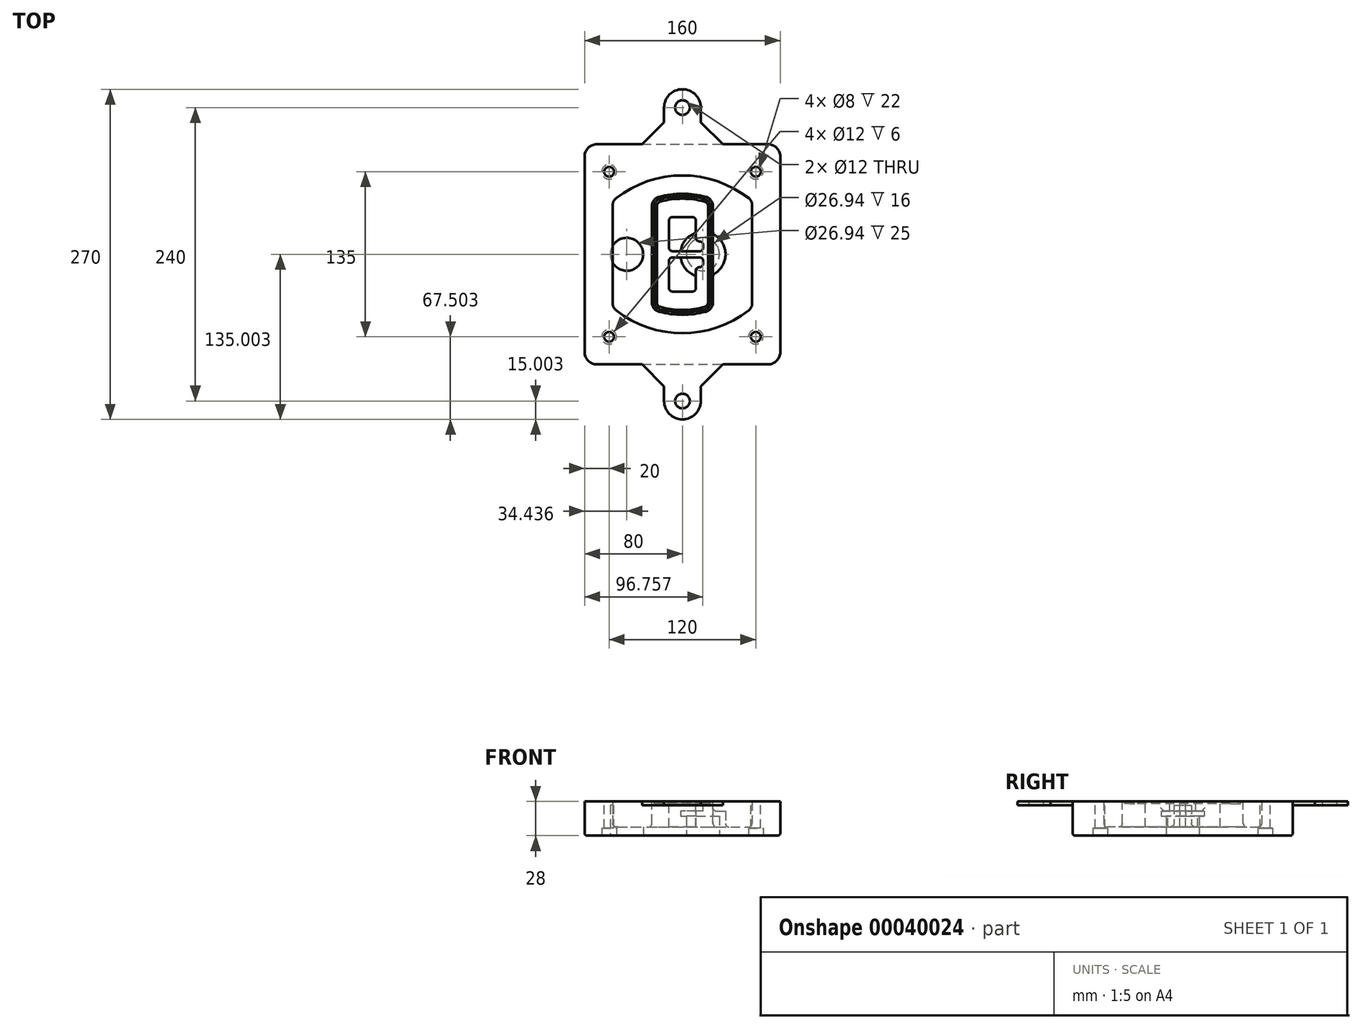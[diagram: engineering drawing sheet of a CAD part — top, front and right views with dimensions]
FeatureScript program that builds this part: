
annotation { "Feature Type Name" : "Feature", "Feature Type Description" : "" }
export const myFeature = defineFeature(function(context is Context, id is Id, definition is map)
    precondition{}
    {
        {
            var Q0;
            Q0=qCreatedBy(makeId("Top.planeOp"),FACE);
            var sketch = newSketch(context, id + "F0", { "sketchPlane" : qUnion([Q0])});
            skPoint(sketch, "E0.rect.middle", {"position": v(0, 0) * mm});
            skLineSegment(sketch, "E1.bottom", {"start": v(24.05, 28.38) * mm, "end": v(164.05, 28.38) * mm});
            skLineSegment(sketch, "E1.top", {"start": v(24.05, 208.38) * mm, "end": v(164.05, 208.38) * mm});
            skLineSegment(sketch, "E1.left", {"start": v(14.05, 38.38) * mm, "end": v(14.05, 198.38) * mm});
            skLineSegment(sketch, "E1.right", {"start": v(174.05, 38.38) * mm, "end": v(174.05, 198.38) * mm});
            skLineSegment(sketch, "E2", {"start": v(14.05, 208.38) * mm, "end": v(174.05, 28.38) * mm, "construction": true});
            skLineSegment(sketch, "E3", {"start": v(174.05, 208.38) * mm, "end": v(14.05, 28.38) * mm, "construction": true});
            skCircle(sketch, "E4", {"center": v(34.05, 185.88) * mm, "radius": 4 * mm});
            skCircle(sketch, "E5", {"center": v(154.05, 185.88) * mm, "radius": 4 * mm});
            skCircle(sketch, "E6", {"center": v(154.05, 50.88) * mm, "radius": 4 * mm});
            skCircle(sketch, "E7", {"center": v(34.05, 50.88) * mm, "radius": 4 * mm});
            skLineSegment(sketch, "E8", {"start": v(34.05, 185.88) * mm, "end": v(154.05, 185.88) * mm, "construction": true});
            skLineSegment(sketch, "E9", {"start": v(154.05, 185.88) * mm, "end": v(154.05, 50.88) * mm, "construction": true});
            skLineSegment(sketch, "E10", {"start": v(154.05, 50.88) * mm, "end": v(34.05, 50.88) * mm, "construction": true});
            skLineSegment(sketch, "E11", {"start": v(34.05, 50.88) * mm, "end": v(34.05, 185.88) * mm, "construction": true});
            skLineSegment(sketch, "E12", {"start": v(34.05, 158.68) * mm, "end": v(34.05, 78.09) * mm});
            skLineSegment(sketch, "E13", {"start": v(154.05, 158.68) * mm, "end": v(154.05, 78.09) * mm});
            skArc(sketch, "E14", {"start": v(150.2, 166.56) * mm, "mid": v(94.05, 185.88) * mm, "end": v(37.9, 166.56) * mm});
            skArc(sketch, "E15", {"start": v(37.9, 70.2) * mm, "mid": v(94.05, 50.88) * mm, "end": v(150.2, 70.2) * mm});
            skLineSegment(sketch, "E16", {"start": v(34.05, 118.38) * mm, "end": v(154.05, 118.38) * mm, "construction": true});
            skPoint(sketch, "E17.visualSharp", {"position": v(34.05, 73.38) * mm});
            skArc(sketch, "E17.filletArc", {"start": v(34.05, 78.09) * mm, "mid": v(35.06, 73.7) * mm, "end": v(37.9, 70.2) * mm});
            skPoint(sketch, "E18.visualSharp", {"position": v(34.05, 163.38) * mm});
            skArc(sketch, "E18.filletArc", {"start": v(37.9, 166.56) * mm, "mid": v(35.06, 163.06) * mm, "end": v(34.05, 158.68) * mm});
            skPoint(sketch, "E19.visualSharp", {"position": v(154.05, 163.38) * mm});
            skArc(sketch, "E19.filletArc", {"start": v(154.05, 158.68) * mm, "mid": v(153.04, 163.06) * mm, "end": v(150.2, 166.56) * mm});
            skPoint(sketch, "E20.visualSharp", {"position": v(154.05, 73.38) * mm});
            skArc(sketch, "E20.filletArc", {"start": v(150.2, 70.2) * mm, "mid": v(153.04, 73.7) * mm, "end": v(154.05, 78.09) * mm});
            skPoint(sketch, "E21.visualSharp", {"position": v(14.05, 208.38) * mm});
            skArc(sketch, "E21.filletArc", {"start": v(24.05, 208.38) * mm, "mid": v(16.98, 205.45) * mm, "end": v(14.05, 198.38) * mm});
            skPoint(sketch, "E22.visualSharp", {"position": v(174.05, 208.38) * mm});
            skArc(sketch, "E22.filletArc", {"start": v(174.05, 198.38) * mm, "mid": v(171.12, 205.45) * mm, "end": v(164.05, 208.38) * mm});
            skPoint(sketch, "E23.visualSharp", {"position": v(174.05, 28.38) * mm});
            skArc(sketch, "E23.filletArc", {"start": v(164.05, 28.38) * mm, "mid": v(171.12, 31.31) * mm, "end": v(174.05, 38.38) * mm});
            skPoint(sketch, "E24.visualSharp", {"position": v(14.05, 28.38) * mm});
            skArc(sketch, "E24.filletArc", {"start": v(14.05, 38.38) * mm, "mid": v(16.98, 31.31) * mm, "end": v(24.05, 28.38) * mm});
            skArc(sketch, "E25.0", {"start": v(151.05, 158.68) * mm, "mid": v(150.34, 161.75) * mm, "end": v(148.36, 164.2) * mm});
            skLineSegment(sketch, "E25.1", {"start": v(151.05, 158.68) * mm, "end": v(151.05, 78.09) * mm});
            skArc(sketch, "E25.2", {"start": v(148.36, 72.57) * mm, "mid": v(150.34, 75.02) * mm, "end": v(151.05, 78.09) * mm});
            skArc(sketch, "E25.3", {"start": v(39.74, 72.57) * mm, "mid": v(94.05, 53.88) * mm, "end": v(148.36, 72.57) * mm});
            skArc(sketch, "E25.4", {"start": v(37.05, 78.09) * mm, "mid": v(37.76, 75.02) * mm, "end": v(39.74, 72.57) * mm});
            skArc(sketch, "E25.5", {"start": v(148.36, 164.2) * mm, "mid": v(94.05, 182.88) * mm, "end": v(39.74, 164.2) * mm});
            skLineSegment(sketch, "E25.6", {"start": v(37.05, 158.68) * mm, "end": v(37.05, 78.09) * mm});
            skArc(sketch, "E25.7", {"start": v(39.74, 164.2) * mm, "mid": v(37.76, 161.75) * mm, "end": v(37.05, 158.68) * mm});
            skArc(sketch, "E26.0", {"start": v(35.43, 169.71) * mm, "mid": v(31.47, 164.82) * mm, "end": v(30.05, 158.68) * mm});
            skArc(sketch, "E26.1", {"start": v(152.67, 169.71) * mm, "mid": v(94.05, 189.88) * mm, "end": v(35.43, 169.71) * mm});
            skArc(sketch, "E26.2", {"start": v(158.05, 158.68) * mm, "mid": v(156.63, 164.82) * mm, "end": v(152.67, 169.71) * mm});
            skLineSegment(sketch, "E26.3", {"start": v(158.05, 158.68) * mm, "end": v(158.05, 78.09) * mm});
            skArc(sketch, "E26.4", {"start": v(152.67, 67.05) * mm, "mid": v(156.63, 71.95) * mm, "end": v(158.05, 78.09) * mm});
            skLineSegment(sketch, "E26.5", {"start": v(30.05, 158.68) * mm, "end": v(30.05, 78.09) * mm});
            skArc(sketch, "E26.6", {"start": v(35.43, 67.05) * mm, "mid": v(94.05, 46.88) * mm, "end": v(152.67, 67.05) * mm});
            skArc(sketch, "E26.7", {"start": v(30.05, 78.09) * mm, "mid": v(31.47, 71.95) * mm, "end": v(35.43, 67.05) * mm});
            skSolve(sketch);
        }
        {
            var Q0;
            Q0=makeQuery(id+"F0.imprint","IMPRINT",FACE,{"disambiguationData":[TD([[makeQuery(id+"F0.imprint","IMPRINT",EDGE,{"derivedFrom":sQuery(id+"F0.wireOp",EDGE,"E1.bottom")}),1.0]])]});
            var Q1;
            Q1=makeQuery(id+"F0.imprint","IMPRINT",FACE,{"disambiguationData":[TD([[makeQuery(id+"F0.imprint","IMPRINT",EDGE,{"derivedFrom":sQuery(id+"F0.wireOp",EDGE,"E12")}),1.0]])]});
            var Q2;
            Q2=makeQuery(id+"F0.imprint","IMPRINT",FACE,{"disambiguationData":[TD([[makeQuery(id+"F0.imprint","IMPRINT",EDGE,{"derivedFrom":sQuery(id+"F0.wireOp",EDGE,"E25.0")}),1.0]])]});
            var Q3;
            Q3=makeQuery(id+"F0.imprint","IMPRINT",FACE,{"disambiguationData":[TD([[makeQuery(id+"F0.imprint","IMPRINT",EDGE,{"derivedFrom":sQuery(id+"F0.wireOp",EDGE,"E12")}),-1.0]])]});
            extrude(context, id + "F1", {"entities" : qUnion([Q0, Q1, Q2, Q3]), "oppositeDirection" : true, "depth" : 25 * mm});
        }
        {
            var Q0;
            Q0=makeQuery(id+"F0.imprint","IMPRINT",FACE,{"disambiguationData":[TD([[makeQuery(id+"F0.imprint","IMPRINT",EDGE,{"derivedFrom":sQuery(id+"F0.wireOp",EDGE,"E12")}),1.0]])]});
            extrude(context, id + "F2", {"entities" : qUnion([Q0]), "operationType" : NewBodyOperationType.ADD, "depth" : 3 * mm});
        }
        {
            var Q0;
            Q0=makeQuery(id+"F0.imprint","IMPRINT",FACE,{"disambiguationData":[TD([[makeQuery(id+"F0.imprint","IMPRINT",EDGE,{"derivedFrom":sQuery(id+"F0.wireOp",EDGE,"E25.0")}),1.0]])]});
            extrude(context, id + "F3", {"entities" : qUnion([Q0]), "operationType" : NewBodyOperationType.REMOVE, "oppositeDirection" : true, "depth" : 18 * mm});
        }
        {
            var Q0;
            Q0=makeQuery(id+"F2.opExtrude","CAP_FACE",FACE,{"disambiguationData":[OSD([sQuery(id+"F0.wireOp",EDGE,"E12"),sQuery(id+"F0.wireOp",EDGE,"E13"),sQuery(id+"F0.wireOp",EDGE,"E14"),sQuery(id+"F0.wireOp",EDGE,"E15"),sQuery(id+"F0.wireOp",EDGE,"E17.filletArc"),sQuery(id+"F0.wireOp",EDGE,"E18.filletArc"),sQuery(id+"F0.wireOp",EDGE,"E19.filletArc"),sQuery(id+"F0.wireOp",EDGE,"E20.filletArc"),sQuery(id+"F0.wireOp",EDGE,"E25.0"),sQuery(id+"F0.wireOp",EDGE,"E25.1"),sQuery(id+"F0.wireOp",EDGE,"E25.2"),sQuery(id+"F0.wireOp",EDGE,"E25.3"),sQuery(id+"F0.wireOp",EDGE,"E25.4"),sQuery(id+"F0.wireOp",EDGE,"E25.5"),sQuery(id+"F0.wireOp",EDGE,"E25.6"),sQuery(id+"F0.wireOp",EDGE,"E25.7")])],"isStart":false});
            var sketch = newSketch(context, id + "F4", { "sketchPlane" : qUnion([Q0])});
            skArc(sketch, "E27.0", {"start": v(74.97, 71.41) * mm, "mid": v(94.05, 68.88) * mm, "end": v(113.13, 71.41) * mm});
            skArc(sketch, "E28.0", {"start": v(113.13, 165.35) * mm, "mid": v(94.05, 167.88) * mm, "end": v(74.97, 165.35) * mm});
            skLineSegment(sketch, "E29", {"start": v(69.05, 157.63) * mm, "end": v(69.05, 79.14) * mm});
            skLineSegment(sketch, "E30", {"start": v(119.05, 157.63) * mm, "end": v(119.05, 79.14) * mm});
            skLineSegment(sketch, "E31", {"start": v(69.05, 163.48) * mm, "end": v(119.05, 163.48) * mm, "construction": true});
            skLineSegment(sketch, "E32", {"start": v(69.05, 73.28) * mm, "end": v(119.05, 73.28) * mm, "construction": true});
            skPoint(sketch, "E33.visualSharp", {"position": v(69.05, 163.48) * mm});
            skArc(sketch, "E33.filletArc", {"start": v(74.97, 165.35) * mm, "mid": v(70.7, 162.5) * mm, "end": v(69.05, 157.63) * mm});
            skPoint(sketch, "E34.visualSharp", {"position": v(119.05, 163.48) * mm});
            skArc(sketch, "E34.filletArc", {"start": v(119.05, 157.63) * mm, "mid": v(117.4, 162.5) * mm, "end": v(113.13, 165.35) * mm});
            skPoint(sketch, "E35.visualSharp", {"position": v(119.05, 73.28) * mm});
            skArc(sketch, "E35.filletArc", {"start": v(113.13, 71.41) * mm, "mid": v(117.4, 74.27) * mm, "end": v(119.05, 79.14) * mm});
            skPoint(sketch, "E36.visualSharp", {"position": v(69.05, 73.28) * mm});
            skArc(sketch, "E36.filletArc", {"start": v(69.05, 79.14) * mm, "mid": v(70.7, 74.27) * mm, "end": v(74.97, 71.41) * mm});
            skArc(sketch, "E37.0", {"start": v(148.36, 164.2) * mm, "mid": v(94.05, 182.88) * mm, "end": v(39.74, 164.2) * mm});
            skArc(sketch, "E37.1", {"start": v(39.74, 164.2) * mm, "mid": v(37.76, 161.75) * mm, "end": v(37.05, 158.68) * mm});
            skLineSegment(sketch, "E37.2", {"start": v(37.05, 158.68) * mm, "end": v(37.05, 78.09) * mm});
            skArc(sketch, "E37.3", {"start": v(37.05, 78.09) * mm, "mid": v(37.76, 75.02) * mm, "end": v(39.74, 72.57) * mm});
            skArc(sketch, "E37.4", {"start": v(39.74, 72.57) * mm, "mid": v(94.05, 53.88) * mm, "end": v(148.36, 72.57) * mm});
            skArc(sketch, "E37.5", {"start": v(148.36, 72.57) * mm, "mid": v(150.34, 75.02) * mm, "end": v(151.05, 78.09) * mm});
            skLineSegment(sketch, "E37.6", {"start": v(151.05, 158.68) * mm, "end": v(151.05, 78.09) * mm});
            skArc(sketch, "E37.7", {"start": v(151.05, 158.68) * mm, "mid": v(150.34, 161.75) * mm, "end": v(148.36, 164.2) * mm});
            skLineSegment(sketch, "E38.0", {"start": v(117.05, 157.63) * mm, "end": v(117.05, 79.14) * mm});
            skArc(sketch, "E38.1", {"start": v(112.61, 73.34) * mm, "mid": v(115.81, 75.49) * mm, "end": v(117.05, 79.14) * mm});
            skArc(sketch, "E38.2", {"start": v(75.49, 73.34) * mm, "mid": v(94.05, 70.88) * mm, "end": v(112.61, 73.34) * mm});
            skArc(sketch, "E38.3", {"start": v(71.05, 79.14) * mm, "mid": v(72.29, 75.49) * mm, "end": v(75.49, 73.34) * mm});
            skLineSegment(sketch, "E38.4", {"start": v(71.05, 157.63) * mm, "end": v(71.05, 79.14) * mm});
            skArc(sketch, "E38.5", {"start": v(117.05, 157.63) * mm, "mid": v(115.81, 161.28) * mm, "end": v(112.61, 163.42) * mm});
            skArc(sketch, "E38.6", {"start": v(75.49, 163.42) * mm, "mid": v(72.29, 161.28) * mm, "end": v(71.05, 157.63) * mm});
            skArc(sketch, "E38.7", {"start": v(112.61, 163.42) * mm, "mid": v(94.05, 165.88) * mm, "end": v(75.49, 163.42) * mm});
            skArc(sketch, "E39.0", {"start": v(115.05, 157.63) * mm, "mid": v(114.23, 160.06) * mm, "end": v(112.1, 161.5) * mm});
            skLineSegment(sketch, "E39.1", {"start": v(115.05, 157.63) * mm, "end": v(115.05, 79.14) * mm});
            skArc(sketch, "E39.2", {"start": v(112.1, 75.27) * mm, "mid": v(114.23, 76.7) * mm, "end": v(115.05, 79.14) * mm});
            skArc(sketch, "E39.3", {"start": v(76, 75.27) * mm, "mid": v(94.05, 72.88) * mm, "end": v(112.1, 75.27) * mm});
            skArc(sketch, "E39.4", {"start": v(73.05, 79.14) * mm, "mid": v(73.87, 76.7) * mm, "end": v(76, 75.27) * mm});
            skArc(sketch, "E39.5", {"start": v(112.1, 161.5) * mm, "mid": v(94.05, 163.88) * mm, "end": v(76, 161.5) * mm});
            skLineSegment(sketch, "E39.6", {"start": v(73.05, 157.63) * mm, "end": v(73.05, 79.14) * mm});
            skArc(sketch, "E39.7", {"start": v(76, 161.5) * mm, "mid": v(73.87, 160.06) * mm, "end": v(73.05, 157.63) * mm});
            skLineSegment(sketch, "E40", {"start": v(69.05, 118.38) * mm, "end": v(119.05, 118.38) * mm, "construction": true});
            skLineSegment(sketch, "E41", {"start": v(83.05, 123.88) * mm, "end": v(83.05, 145.88) * mm});
            skLineSegment(sketch, "E42", {"start": v(86.05, 148.88) * mm, "end": v(102.05, 148.88) * mm});
            skLineSegment(sketch, "E43", {"start": v(105.05, 145.88) * mm, "end": v(105.05, 131.88) * mm});
            skLineSegment(sketch, "E44", {"start": v(108.05, 128.88) * mm, "end": v(108.05, 128.88) * mm});
            skLineSegment(sketch, "E45", {"start": v(111.05, 125.88) * mm, "end": v(111.05, 123.88) * mm});
            skLineSegment(sketch, "E46", {"start": v(108.05, 120.88) * mm, "end": v(86.05, 120.88) * mm});
            skPoint(sketch, "E47.visualSharp", {"position": v(83.05, 148.88) * mm});
            skArc(sketch, "E47.filletArc", {"start": v(86.05, 148.88) * mm, "mid": v(83.93, 148) * mm, "end": v(83.05, 145.88) * mm});
            skPoint(sketch, "E48.visualSharp", {"position": v(105.05, 148.88) * mm});
            skArc(sketch, "E48.filletArc", {"start": v(105.05, 145.88) * mm, "mid": v(104.17, 148) * mm, "end": v(102.05, 148.88) * mm});
            skPoint(sketch, "E49.visualSharp", {"position": v(105.05, 128.88) * mm});
            skArc(sketch, "E49.filletArc", {"start": v(105.05, 131.88) * mm, "mid": v(105.93, 129.76) * mm, "end": v(108.05, 128.88) * mm});
            skPoint(sketch, "E50.visualSharp", {"position": v(111.05, 128.88) * mm});
            skArc(sketch, "E50.filletArc", {"start": v(111.05, 125.88) * mm, "mid": v(110.17, 128) * mm, "end": v(108.05, 128.88) * mm});
            skPoint(sketch, "E51.visualSharp", {"position": v(111.05, 120.88) * mm});
            skArc(sketch, "E51.filletArc", {"start": v(108.05, 120.88) * mm, "mid": v(110.17, 121.76) * mm, "end": v(111.05, 123.88) * mm});
            skPoint(sketch, "E52.visualSharp", {"position": v(83.05, 120.88) * mm});
            skArc(sketch, "E52.filletArc", {"start": v(83.05, 123.88) * mm, "mid": v(83.93, 121.76) * mm, "end": v(86.05, 120.88) * mm});
            skLineSegment(sketch, "E53.0.MirrorCS", {"start": v(108.05, 115.88) * mm, "end": v(86.05, 115.88) * mm});
            skArc(sketch, "E54.0.MirrorCS", {"start": v(83.05, 112.88) * mm, "mid": v(83.93, 115) * mm, "end": v(86.05, 115.88) * mm});
            skLineSegment(sketch, "E55.0.MirrorCS", {"start": v(83.05, 112.88) * mm, "end": v(83.05, 90.88) * mm});
            skArc(sketch, "E56.0.MirrorCS", {"start": v(86.05, 87.88) * mm, "mid": v(83.93, 88.76) * mm, "end": v(83.05, 90.88) * mm});
            skLineSegment(sketch, "E57.0.MirrorCS", {"start": v(86.05, 87.88) * mm, "end": v(102.05, 87.88) * mm});
            skArc(sketch, "E58.0.MirrorCS", {"start": v(105.05, 90.88) * mm, "mid": v(104.17, 88.76) * mm, "end": v(102.05, 87.88) * mm});
            skLineSegment(sketch, "E59.0.MirrorCS", {"start": v(105.05, 90.88) * mm, "end": v(105.05, 104.88) * mm});
            skArc(sketch, "E60.0.MirrorCS", {"start": v(105.05, 104.88) * mm, "mid": v(105.93, 107) * mm, "end": v(108.05, 107.88) * mm});
            skArc(sketch, "E61.0.MirrorCS", {"start": v(111.05, 110.88) * mm, "mid": v(110.17, 108.76) * mm, "end": v(108.05, 107.88) * mm});
            skLineSegment(sketch, "E62.0.MirrorCS", {"start": v(111.05, 110.88) * mm, "end": v(111.05, 112.88) * mm});
            skArc(sketch, "E63.0.MirrorCS", {"start": v(108.05, 115.88) * mm, "mid": v(110.17, 115) * mm, "end": v(111.05, 112.88) * mm});
            skSolve(sketch);
        }
        {
            var Q0;
            Q0=makeQuery(id+"F4.imprint","IMPRINT",FACE,{"disambiguationData":[TD([[makeQuery(id+"F4.imprint","IMPRINT",EDGE,{"derivedFrom":sQuery(id+"F4.wireOp",EDGE,"E27.0")}),1.0]])]});
            var Q1;
            Q1=makeQuery(id+"F4.imprint","IMPRINT",FACE,{"disambiguationData":[TD([[makeQuery(id+"F4.imprint","IMPRINT",EDGE,{"derivedFrom":sQuery(id+"F4.wireOp",EDGE,"E38.0")}),-1.0]])]});
            var Q2;
            Q2=makeQuery(id+"F4.imprint","IMPRINT",FACE,{"disambiguationData":[TD([[makeQuery(id+"F4.imprint","IMPRINT",EDGE,{"derivedFrom":sQuery(id+"F4.wireOp",EDGE,"E39.0")}),1.0]])]});
            extrude(context, id + "F5", {"entities" : qUnion([Q0, Q1, Q2]), "operationType" : NewBodyOperationType.ADD, "endBound" : BoundingType.UP_TO_NEXT, "oppositeDirection" : true, "depth" : 25 * mm});
        }
        {
            var Q0;
            Q0=makeQuery(id+"F4.imprint","IMPRINT",FACE,{"disambiguationData":[TD([[makeQuery(id+"F4.imprint","IMPRINT",EDGE,{"derivedFrom":sQuery(id+"F4.wireOp",EDGE,"E38.0")}),-1.0]])]});
            extrude(context, id + "F6", {"entities" : qUnion([Q0]), "operationType" : NewBodyOperationType.REMOVE, "oppositeDirection" : true, "depth" : 2 * mm});
        }
        {
            var Q0;
            Q0=makeQuery(id+"F1.opExtrude","CAP_FACE",FACE,{"disambiguationData":[OSD([sQuery(id+"F0.wireOp",EDGE,"E1.bottom"),sQuery(id+"F0.wireOp",EDGE,"E1.top"),sQuery(id+"F0.wireOp",EDGE,"E1.left"),sQuery(id+"F0.wireOp",EDGE,"E1.right"),sQuery(id+"F0.wireOp",EDGE,"E4"),sQuery(id+"F0.wireOp",EDGE,"E5"),sQuery(id+"F0.wireOp",EDGE,"E6"),sQuery(id+"F0.wireOp",EDGE,"E7"),sQuery(id+"F0.wireOp",EDGE,"E21.filletArc"),sQuery(id+"F0.wireOp",EDGE,"E22.filletArc"),sQuery(id+"F0.wireOp",EDGE,"E23.filletArc"),sQuery(id+"F0.wireOp",EDGE,"E24.filletArc")])],"isStart":false});
            var sketch = newSketch(context, id + "F7", { "sketchPlane" : qUnion([Q0])});
            skCircle(sketch, "E64", {"center": v(110.8, -118.38) * mm, "radius": 13.47 * mm});
            skCircle(sketch, "E65", {"center": v(48.49, -118.38) * mm, "radius": 13.47 * mm});
            skLineSegment(sketch, "E66", {"start": v(174.05, -118.38) * mm, "end": v(14.05, -118.38) * mm});
            skCircle(sketch, "E67", {"center": v(110.8, -118.38) * mm, "radius": 18.47 * mm});
            skCircle(sketch, "E68", {"center": v(154.05, -185.88) * mm, "radius": 6 * mm});
            skCircle(sketch, "E69", {"center": v(34.05, -185.88) * mm, "radius": 6 * mm});
            skCircle(sketch, "E70", {"center": v(34.05, -50.88) * mm, "radius": 6 * mm});
            skCircle(sketch, "E71", {"center": v(154.05, -50.88) * mm, "radius": 6 * mm});
            skSolve(sketch);
        }
        {
            var Q0;
            {var subQ1=sQuery(id+"F7.wireOp",EDGE,"E66");var subQ4=sQuery(id+"F7.wireOp",EDGE,"E64");var subQ6=makeQuery(id+"F7.imprint","INTERSECT",VERTEX,{"disambiguationData":[OD(0.0)],"derivedFrom":[subQ4,subQ1]});Q0=makeQuery(id+"F7.imprint","IMPRINT",FACE,{"disambiguationData":[TD([[makeQuery(id+"F7.imprint","IMPRINT",EDGE,{"disambiguationData":[TD([[subQ6,-1.0]])],"derivedFrom":subQ4}),-1.0]])]});}
            var Q1;
            {var subQ0=sQuery(id+"F7.wireOp",EDGE,"E66");var subQ1=sQuery(id+"F7.wireOp",EDGE,"E64");var subQ3=makeQuery(id+"F7.imprint","INTERSECT",VERTEX,{"disambiguationData":[OD(0.0)],"derivedFrom":[subQ1,subQ0]});Q1=makeQuery(id+"F7.imprint","IMPRINT",FACE,{"disambiguationData":[TD([[makeQuery(id+"F7.imprint","IMPRINT",EDGE,{"disambiguationData":[TD([[subQ3,-1.0]])],"derivedFrom":subQ1}),1.0]])]});}
            var Q2;
            {var subQ0=sQuery(id+"F7.wireOp",EDGE,"E66");var subQ1=sQuery(id+"F7.wireOp",EDGE,"E64");var subQ3=makeQuery(id+"F7.imprint","INTERSECT",VERTEX,{"disambiguationData":[OD(0.0)],"derivedFrom":[subQ1,subQ0]});Q2=makeQuery(id+"F7.imprint","IMPRINT",FACE,{"disambiguationData":[TD([[makeQuery(id+"F7.imprint","IMPRINT",EDGE,{"disambiguationData":[TD([[subQ3,1.0]])],"derivedFrom":subQ1}),1.0]])]});}
            var Q3;
            {var subQ1=sQuery(id+"F7.wireOp",EDGE,"E66");var subQ4=sQuery(id+"F7.wireOp",EDGE,"E64");var subQ6=makeQuery(id+"F7.imprint","INTERSECT",VERTEX,{"disambiguationData":[OD(0.0)],"derivedFrom":[subQ4,subQ1]});Q3=makeQuery(id+"F7.imprint","IMPRINT",FACE,{"disambiguationData":[TD([[makeQuery(id+"F7.imprint","IMPRINT",EDGE,{"disambiguationData":[TD([[subQ6,1.0]])],"derivedFrom":subQ4}),-1.0]])]});}
            extrude(context, id + "F8", {"entities" : qUnion([Q0, Q1, Q2, Q3]), "operationType" : NewBodyOperationType.ADD, "oppositeDirection" : true, "depth" : 20 * mm});
        }
        {
            var Q0;
            {var subQ0=sQuery(id+"F7.wireOp",EDGE,"E66");var subQ1=sQuery(id+"F7.wireOp",EDGE,"E64");var subQ3=makeQuery(id+"F7.imprint","INTERSECT",VERTEX,{"disambiguationData":[OD(0.0)],"derivedFrom":[subQ1,subQ0]});Q0=makeQuery(id+"F7.imprint","IMPRINT",FACE,{"disambiguationData":[TD([[makeQuery(id+"F7.imprint","IMPRINT",EDGE,{"disambiguationData":[TD([[subQ3,-1.0]])],"derivedFrom":subQ1}),1.0]])]});}
            var Q1;
            {var subQ0=sQuery(id+"F7.wireOp",EDGE,"E66");var subQ1=sQuery(id+"F7.wireOp",EDGE,"E64");var subQ3=makeQuery(id+"F7.imprint","INTERSECT",VERTEX,{"disambiguationData":[OD(0.0)],"derivedFrom":[subQ1,subQ0]});Q1=makeQuery(id+"F7.imprint","IMPRINT",FACE,{"disambiguationData":[TD([[makeQuery(id+"F7.imprint","IMPRINT",EDGE,{"disambiguationData":[TD([[subQ3,1.0]])],"derivedFrom":subQ1}),1.0]])]});}
            extrude(context, id + "F9", {"entities" : qUnion([Q0, Q1]), "operationType" : NewBodyOperationType.REMOVE, "oppositeDirection" : true, "depth" : 16 * mm});
        }
        {
            var Q0;
            {var subQ0=sQuery(id+"F7.wireOp",EDGE,"E66");var subQ1=sQuery(id+"F7.wireOp",EDGE,"E65");var subQ3=makeQuery(id+"F7.imprint","INTERSECT",VERTEX,{"disambiguationData":[OD(0.0)],"derivedFrom":[subQ1,subQ0]});Q0=makeQuery(id+"F7.imprint","IMPRINT",FACE,{"disambiguationData":[TD([[makeQuery(id+"F7.imprint","IMPRINT",EDGE,{"disambiguationData":[TD([[subQ3,-1.0]])],"derivedFrom":subQ1}),1.0]])]});}
            var Q1;
            {var subQ0=sQuery(id+"F7.wireOp",EDGE,"E66");var subQ1=sQuery(id+"F7.wireOp",EDGE,"E65");var subQ3=makeQuery(id+"F7.imprint","INTERSECT",VERTEX,{"disambiguationData":[OD(0.0)],"derivedFrom":[subQ1,subQ0]});Q1=makeQuery(id+"F7.imprint","IMPRINT",FACE,{"disambiguationData":[TD([[makeQuery(id+"F7.imprint","IMPRINT",EDGE,{"disambiguationData":[TD([[subQ3,1.0]])],"derivedFrom":subQ1}),1.0]])]});}
            extrude(context, id + "F10", {"entities" : qUnion([Q0, Q1]), "operationType" : NewBodyOperationType.REMOVE, "oppositeDirection" : true, "depth" : 25 * mm});
        }
        {
            var Q0;
            Q0=makeQuery(id+"F7.imprint","IMPRINT",FACE,{"disambiguationData":[TD([[makeQuery(id+"F7.imprint","IMPRINT",EDGE,{"derivedFrom":sQuery(id+"F7.wireOp",EDGE,"E68")}),1.0]])]});
            var Q1;
            Q1=makeQuery(id+"F7.imprint","IMPRINT",FACE,{"disambiguationData":[TD([[makeQuery(id+"F7.imprint","IMPRINT",EDGE,{"derivedFrom":makeQuery(id+"F1.opExtrude","CAP_EDGE",EDGE,{"disambiguationData":[OSD([sQuery(id+"F0.wireOp",EDGE,"E5")])],"isStart":false})}),-1.0]])]});
            var Q2;
            Q2=makeQuery(id+"F7.imprint","IMPRINT",FACE,{"disambiguationData":[TD([[makeQuery(id+"F7.imprint","IMPRINT",EDGE,{"derivedFrom":sQuery(id+"F7.wireOp",EDGE,"E69")}),1.0]])]});
            var Q3;
            Q3=makeQuery(id+"F7.imprint","IMPRINT",FACE,{"disambiguationData":[TD([[makeQuery(id+"F7.imprint","IMPRINT",EDGE,{"derivedFrom":makeQuery(id+"F1.opExtrude","CAP_EDGE",EDGE,{"disambiguationData":[OSD([sQuery(id+"F0.wireOp",EDGE,"E4")])],"isStart":false})}),-1.0]])]});
            var Q4;
            Q4=makeQuery(id+"F7.imprint","IMPRINT",FACE,{"disambiguationData":[TD([[makeQuery(id+"F7.imprint","IMPRINT",EDGE,{"derivedFrom":sQuery(id+"F7.wireOp",EDGE,"E70")}),1.0]])]});
            var Q5;
            Q5=makeQuery(id+"F7.imprint","IMPRINT",FACE,{"disambiguationData":[TD([[makeQuery(id+"F7.imprint","IMPRINT",EDGE,{"derivedFrom":makeQuery(id+"F1.opExtrude","CAP_EDGE",EDGE,{"disambiguationData":[OSD([sQuery(id+"F0.wireOp",EDGE,"E7")])],"isStart":false})}),-1.0]])]});
            var Q6;
            Q6=makeQuery(id+"F7.imprint","IMPRINT",FACE,{"disambiguationData":[TD([[makeQuery(id+"F7.imprint","IMPRINT",EDGE,{"derivedFrom":sQuery(id+"F7.wireOp",EDGE,"E71")}),1.0]])]});
            var Q7;
            Q7=makeQuery(id+"F7.imprint","IMPRINT",FACE,{"disambiguationData":[TD([[makeQuery(id+"F7.imprint","IMPRINT",EDGE,{"derivedFrom":makeQuery(id+"F1.opExtrude","CAP_EDGE",EDGE,{"disambiguationData":[OSD([sQuery(id+"F0.wireOp",EDGE,"E6")])],"isStart":false})}),-1.0]])]});
            extrude(context, id + "F11", {"entities" : qUnion([Q0, Q1, Q2, Q3, Q4, Q5, Q6, Q7]), "operationType" : NewBodyOperationType.REMOVE, "oppositeDirection" : true, "depth" : 6 * mm});
        }
        {
            var Q0;
            Q0=makeQuery(id+"F9.boolean.opBoolean","COPY",FACE,{"derivedFrom":makeQuery(id+"F9.opExtrude","CAP_FACE",FACE,{"disambiguationData":[OSD([sQuery(id+"F7.wireOp",EDGE,"E64")])],"isStart":false})});
            var sketch = newSketch(context, id + "F12", { "sketchPlane" : qUnion([Q0])});
            skArc(sketch, "E72.0", {"start": v(105.05, -100.83) * mm, "mid": v(96.62, -106.56) * mm, "end": v(92.5, -115.88) * mm});
            skArc(sketch, "E72.1", {"start": v(92.5, -120.88) * mm, "mid": v(96.62, -130.2) * mm, "end": v(105.05, -135.93) * mm});
            skLineSegment(sketch, "E73", {"start": v(92.5, -120.88) * mm, "end": v(108.05, -120.88) * mm});
            skLineSegment(sketch, "E74.0", {"start": v(108.05, -115.88) * mm, "end": v(92.5, -115.88) * mm});
            skArc(sketch, "E74.1", {"start": v(108.05, -115.88) * mm, "mid": v(110.17, -115) * mm, "end": v(111.05, -112.88) * mm});
            skLineSegment(sketch, "E74.2", {"start": v(111.05, -110.88) * mm, "end": v(111.05, -112.88) * mm});
            skArc(sketch, "E74.3", {"start": v(111.05, -110.88) * mm, "mid": v(110.17, -108.76) * mm, "end": v(108.05, -107.88) * mm});
            skArc(sketch, "E74.4", {"start": v(105.05, -104.88) * mm, "mid": v(105.93, -107) * mm, "end": v(108.05, -107.88) * mm});
            skLineSegment(sketch, "E74.5", {"start": v(105.05, -100.83) * mm, "end": v(105.05, -104.88) * mm});
            skLineSegment(sketch, "E74.7", {"start": v(108.05, -120.88) * mm, "end": v(92.5, -120.88) * mm});
            skArc(sketch, "E74.8", {"start": v(108.05, -120.88) * mm, "mid": v(110.17, -121.76) * mm, "end": v(111.05, -123.88) * mm});
            skLineSegment(sketch, "E74.9", {"start": v(111.05, -125.88) * mm, "end": v(111.05, -123.88) * mm});
            skArc(sketch, "E74.10", {"start": v(111.05, -125.88) * mm, "mid": v(110.17, -128) * mm, "end": v(108.05, -128.88) * mm});
            skArc(sketch, "E74.11", {"start": v(105.05, -131.88) * mm, "mid": v(105.93, -129.76) * mm, "end": v(108.05, -128.88) * mm});
            skLineSegment(sketch, "E74.12", {"start": v(105.05, -135.93) * mm, "end": v(105.05, -131.88) * mm});
            skPoint(sketch, "E75.orphan", {"position": v(105.05, -145.88) * mm});
            skPoint(sketch, "E76.orphan", {"position": v(86.05, -120.88) * mm});
            skPoint(sketch, "E77.orphan", {"position": v(86.05, -115.88) * mm});
            skPoint(sketch, "E78.orphan", {"position": v(105.05, -90.88) * mm});
            skSolve(sketch);
        }
        {
            var Q0;
            {var subQ7=sQuery(id+"F12.wireOp",EDGE,"E72.0");var subQ14=sQuery(id+"F12.wireOp",EDGE,"E72.1");var subQ16=sQuery(id+"F12.wireOp",EDGE,"E74.1");var subQ18=sQuery(id+"F12.wireOp",EDGE,"E74.8");Q0=qUnion([makeQuery(id+"F12.imprint","IMPRINT",FACE,{"disambiguationData":[TD([[makeQuery(id+"F12.imprint","IMPRINT",EDGE,{"derivedFrom":subQ7}),1.0]])]}),makeQuery(id+"F12.imprint","IMPRINT",FACE,{"disambiguationData":[TD([[makeQuery(id+"F12.imprint","IMPRINT",EDGE,{"derivedFrom":subQ14}),1.0]])]}),makeQuery(id+"F12.imprint","IMPRINT",FACE,{"disambiguationData":[TD([[makeQuery(id+"F12.imprint","IMPRINT",EDGE,{"derivedFrom":subQ16}),1.0]])]}),makeQuery(id+"F12.imprint","IMPRINT",FACE,{"disambiguationData":[TD([[makeQuery(id+"F12.imprint","IMPRINT",EDGE,{"derivedFrom":subQ18}),-1.0]])]})]);}
            var Q1;
            Q1=makeQuery(id+"F5.boolean.opBoolean","SPLIT",FACE,{"disambiguationData":[TD([makeQuery(id+"F5.opExtrude","SWEPT_FACE",FACE,{"disambiguationData":[OSD([sQuery(id+"F4.wireOp",EDGE,"E41")])]})])],"derivedFrom":makeQuery(id+"F3.boolean.opBoolean","COPY",FACE,{"derivedFrom":makeQuery(id+"F3.opExtrude","CAP_FACE",FACE,{"disambiguationData":[OSD([sQuery(id+"F0.wireOp",EDGE,"E25.0"),sQuery(id+"F0.wireOp",EDGE,"E25.1"),sQuery(id+"F0.wireOp",EDGE,"E25.2"),sQuery(id+"F0.wireOp",EDGE,"E25.3"),sQuery(id+"F0.wireOp",EDGE,"E25.4"),sQuery(id+"F0.wireOp",EDGE,"E25.5"),sQuery(id+"F0.wireOp",EDGE,"E25.6"),sQuery(id+"F0.wireOp",EDGE,"E25.7")])],"isStart":false})})});
            extrude(context, id + "F13", {"entities" : qUnion([Q0]), "operationType" : NewBodyOperationType.REMOVE, "endBound" : BoundingType.UP_TO_SURFACE, "endBoundEntityFace" : qUnion([Q1]), "depth" : 25 * mm});
        }
        {
            var Q0;
            Q0=makeQuery(id+"F3.boolean.opBoolean","COPY",EDGE,{"derivedFrom":makeQuery(id+"F3.opExtrude","CAP_EDGE",EDGE,{"disambiguationData":[OSD([sQuery(id+"F0.wireOp",EDGE,"E25.6")])],"isStart":false})});
            var Q1;
            Q1=makeQuery(id+"F8.boolean.opBoolean","INTERSECT",EDGE,{"derivedFrom":[makeQuery(id+"F5.opExtrude","SWEPT_FACE",FACE,{"disambiguationData":[OSD([sQuery(id+"F4.wireOp",EDGE,"E30")])]}),makeQuery(id+"F8.opExtrude","CAP_FACE",FACE,{"disambiguationData":[OSD([sQuery(id+"F7.wireOp",EDGE,"E67")])],"isStart":false})]});
            var Q2;
            Q2=makeQuery(id+"F8.boolean.opBoolean","INTERSECT",EDGE,{"disambiguationData":[OD(1.0)],"derivedFrom":[makeQuery(id+"F5.opExtrude","SWEPT_FACE",FACE,{"disambiguationData":[OSD([sQuery(id+"F4.wireOp",EDGE,"E30")])]}),makeQuery(id+"F8.opExtrude","SWEPT_FACE",FACE,{"disambiguationData":[OSD([sQuery(id+"F7.wireOp",EDGE,"E67")])]})]});
            var Q3;
            {var subQ0=sQuery(id+"F4.wireOp",EDGE,"E30");Q3=makeQuery(id+"F8.boolean.opBoolean","SPLIT",EDGE,{"disambiguationData":[TD([makeQuery(id+"F5.opExtrude","SWEPT_FACE",FACE,{"disambiguationData":[OSD([sQuery(id+"F4.wireOp",EDGE,"E35.filletArc")])]})])],"derivedFrom":makeQuery(id+"F5.opExtrude","CAP_EDGE",EDGE,{"disambiguationData":[OSD([subQ0])],"isStart":false})});}
            var Q4;
            {var subQ0=sQuery(id+"F0.wireOp",EDGE,"E25.7");var subQ1=sQuery(id+"F0.wireOp",EDGE,"E25.1");var subQ2=sQuery(id+"F0.wireOp",EDGE,"E25.6");var subQ3=sQuery(id+"F0.wireOp",EDGE,"E25.5");var subQ4=sQuery(id+"F0.wireOp",EDGE,"E25.4");var subQ5=sQuery(id+"F0.wireOp",EDGE,"E25.0");var subQ6=sQuery(id+"F0.wireOp",EDGE,"E25.2");var subQ7=sQuery(id+"F0.wireOp",EDGE,"E25.3");Q4=makeQuery(id+"F8.boolean.opBoolean","INTERSECT",EDGE,{"derivedFrom":[makeQuery(id+"F5.boolean.opBoolean","SPLIT",FACE,{"disambiguationData":[TD([makeQuery(id+"F2.opExtrude","SWEPT_FACE",FACE,{"disambiguationData":[OSD([subQ5])]})])],"derivedFrom":makeQuery(id+"F3.boolean.opBoolean","COPY",FACE,{"derivedFrom":makeQuery(id+"F3.opExtrude","CAP_FACE",FACE,{"disambiguationData":[OSD([subQ5,subQ1,subQ6,subQ7,subQ4,subQ3,subQ2,subQ0])],"isStart":false})})}),makeQuery(id+"F8.opExtrude","SWEPT_FACE",FACE,{"disambiguationData":[OSD([sQuery(id+"F7.wireOp",EDGE,"E67")])]})]});}
            var Q5;
            Q5=makeQuery(id+"F8.boolean.opBoolean","INTERSECT",EDGE,{"disambiguationData":[OD(0.0)],"derivedFrom":[makeQuery(id+"F5.opExtrude","SWEPT_FACE",FACE,{"disambiguationData":[OSD([sQuery(id+"F4.wireOp",EDGE,"E30")])]}),makeQuery(id+"F8.opExtrude","SWEPT_FACE",FACE,{"disambiguationData":[OSD([sQuery(id+"F7.wireOp",EDGE,"E67")])]})]});
            fillet(context, id + "F14", {"entities" : qUnion([Q0, Q1, Q2, Q3, Q4, Q5]), "radius" : 3 * mm, "tangentPropagation" : true, "allowEdgeOverflow" : false});
        }
        {
            var Q0;
            Q0=makeQuery(id+"F1.opExtrude","CAP_EDGE",EDGE,{"disambiguationData":[OSD([sQuery(id+"F0.wireOp",EDGE,"E1.bottom")])],"isStart":false});
            fillet(context, id + "F15", {"entities" : qUnion([Q0]), "radius" : 2 * mm, "tangentPropagation" : true, "allowEdgeOverflow" : false});
        }
        {
            var Q0;
            {var subQ0=sQuery(id+"F0.wireOp",EDGE,"E1.bottom");var subQ1=sQuery(id+"F0.wireOp",EDGE,"E1.top");var subQ2=sQuery(id+"F0.wireOp",EDGE,"E1.left");var subQ3=sQuery(id+"F0.wireOp",EDGE,"E1.right");var subQ4=sQuery(id+"F0.wireOp",EDGE,"E4");var subQ5=sQuery(id+"F0.wireOp",EDGE,"E5");var subQ6=sQuery(id+"F0.wireOp",EDGE,"E6");var subQ7=sQuery(id+"F0.wireOp",EDGE,"E7");var subQ8=sQuery(id+"F0.wireOp",EDGE,"E21.filletArc");var subQ9=sQuery(id+"F0.wireOp",EDGE,"E22.filletArc");var subQ10=sQuery(id+"F0.wireOp",EDGE,"E23.filletArc");var subQ11=sQuery(id+"F0.wireOp",EDGE,"E24.filletArc");Q0=makeQuery(id+"F2.boolean.opBoolean","SPLIT",FACE,{"disambiguationData":[TD([makeQuery(id+"F1.opExtrude","SWEPT_FACE",FACE,{"disambiguationData":[OSD([subQ0])]})])],"derivedFrom":makeQuery(id+"F1.opExtrude","CAP_FACE",FACE,{"disambiguationData":[OSD([subQ0,subQ1,subQ2,subQ3,subQ4,subQ5,subQ6,subQ7,subQ8,subQ9,subQ10,subQ11])],"isStart":true})});}
            var sketch = newSketch(context, id + "F16", { "sketchPlane" : qUnion([Q0])});
            skLineSegment(sketch, "E79", {"start": v(61.05, 208.38) * mm, "end": v(79.05, 226.38) * mm});
            skLineSegment(sketch, "E80", {"start": v(127.05, 208.38) * mm, "end": v(109.05, 226.38) * mm});
            skLineSegment(sketch, "E81", {"start": v(94.05, 238.38) * mm, "end": v(94.05, 208.38) * mm, "construction": true});
            skCircle(sketch, "E82", {"center": v(94.05, 238.38) * mm, "radius": 6 * mm});
            skLineSegment(sketch, "E83", {"start": v(79.05, 226.38) * mm, "end": v(79.05, 238.38) * mm});
            skLineSegment(sketch, "E84", {"start": v(109.05, 226.38) * mm, "end": v(109.05, 238.38) * mm});
            skArc(sketch, "E85", {"start": v(109.05, 238.38) * mm, "mid": v(94.05, 253.38) * mm, "end": v(79.05, 238.38) * mm});
            skLineSegment(sketch, "E86", {"start": v(14.05, 118.38) * mm, "end": v(174.05, 118.38) * mm, "construction": true});
            skArc(sketch, "E87.MirrorCS", {"start": v(79.05, 238.38) * mm, "mid": v(94.05, 253.38) * mm, "end": v(109.05, 238.38) * mm});
            skLineSegment(sketch, "E88.MirrorCS", {"start": v(174.05, 118.38) * mm, "end": v(14.05, 118.38) * mm});
            skLineSegment(sketch, "E89.MirrorCS", {"start": v(109.05, 10.38) * mm, "end": v(109.05, -1.62) * mm});
            skLineSegment(sketch, "E90.MirrorCS", {"start": v(79.05, 10.38) * mm, "end": v(79.05, -1.62) * mm});
            skArc(sketch, "E91.MirrorCS", {"start": v(109.05, -1.62) * mm, "mid": v(94.05, -16.62) * mm, "end": v(79.05, -1.62) * mm});
            skLineSegment(sketch, "E92.MirrorCS", {"start": v(127.05, 28.38) * mm, "end": v(109.05, 10.38) * mm});
            skCircle(sketch, "E93.MirrorC", {"center": v(94.05, -1.62) * mm, "radius": 6 * mm});
            skLineSegment(sketch, "E94.MirrorCS", {"start": v(61.05, 28.38) * mm, "end": v(79.05, 10.38) * mm});
            skArc(sketch, "E95.MirrorCS", {"start": v(79.05, -1.62) * mm, "mid": v(94.05, -16.62) * mm, "end": v(109.05, -1.62) * mm});
            skLineSegment(sketch, "E96.MirrorCS", {"start": v(94.05, -1.62) * mm, "end": v(94.05, 28.38) * mm});
            skSolve(sketch);
        }
        {
            var Q0;
            Q0=makeQuery(id+"F16.imprint","IMPRINT",FACE,{"disambiguationData":[TD([[makeQuery(id+"F16.imprint","IMPRINT",EDGE,{"derivedFrom":sQuery(id+"F16.wireOp",EDGE,"E83")}),-1.0]])]});
            var Q1;
            Q1=makeQuery(id+"F16.imprint","IMPRINT",FACE,{"disambiguationData":[TD([[makeQuery(id+"F16.imprint","IMPRINT",EDGE,{"derivedFrom":sQuery(id+"F16.wireOp",EDGE,"E89.MirrorCS")}),-1.0]])]});
            var Q2;
            Q2=makeQuery(id+"F16.imprint","IMPRINT",FACE,{"disambiguationData":[TD([[makeQuery(id+"F16.imprint","IMPRINT",EDGE,{"derivedFrom":makeQuery(id+"F1.opExtrude","CAP_EDGE",EDGE,{"disambiguationData":[OSD([sQuery(id+"F0.wireOp",EDGE,"E6")])],"isStart":true})}),-1.0]])]});
            var Q3;
            Q3=makeQuery(id+"F16.imprint","IMPRINT",FACE,{"disambiguationData":[TD([[makeQuery(id+"F16.imprint","IMPRINT",EDGE,{"derivedFrom":makeQuery(id+"F1.opExtrude","CAP_EDGE",EDGE,{"disambiguationData":[OSD([sQuery(id+"F0.wireOp",EDGE,"E4")])],"isStart":true})}),-1.0]])]});
            var Q4;
            Q4=makeQuery(id+"F2.opExtrude","CAP_FACE",FACE,{"disambiguationData":[OSD([sQuery(id+"F0.wireOp",EDGE,"E12"),sQuery(id+"F0.wireOp",EDGE,"E13"),sQuery(id+"F0.wireOp",EDGE,"E14"),sQuery(id+"F0.wireOp",EDGE,"E15"),sQuery(id+"F0.wireOp",EDGE,"E17.filletArc"),sQuery(id+"F0.wireOp",EDGE,"E18.filletArc"),sQuery(id+"F0.wireOp",EDGE,"E19.filletArc"),sQuery(id+"F0.wireOp",EDGE,"E20.filletArc"),sQuery(id+"F0.wireOp",EDGE,"E25.0"),sQuery(id+"F0.wireOp",EDGE,"E25.1"),sQuery(id+"F0.wireOp",EDGE,"E25.2"),sQuery(id+"F0.wireOp",EDGE,"E25.3"),sQuery(id+"F0.wireOp",EDGE,"E25.4"),sQuery(id+"F0.wireOp",EDGE,"E25.5"),sQuery(id+"F0.wireOp",EDGE,"E25.6"),sQuery(id+"F0.wireOp",EDGE,"E25.7")])],"isStart":false});
            extrude(context, id + "F17", {"entities" : qUnion([Q0, Q1, Q2, Q3]), "operationType" : NewBodyOperationType.ADD, "endBound" : BoundingType.UP_TO_SURFACE, "endBoundEntityFace" : qUnion([Q4]), "depth" : 25 * mm});
        }
    });
